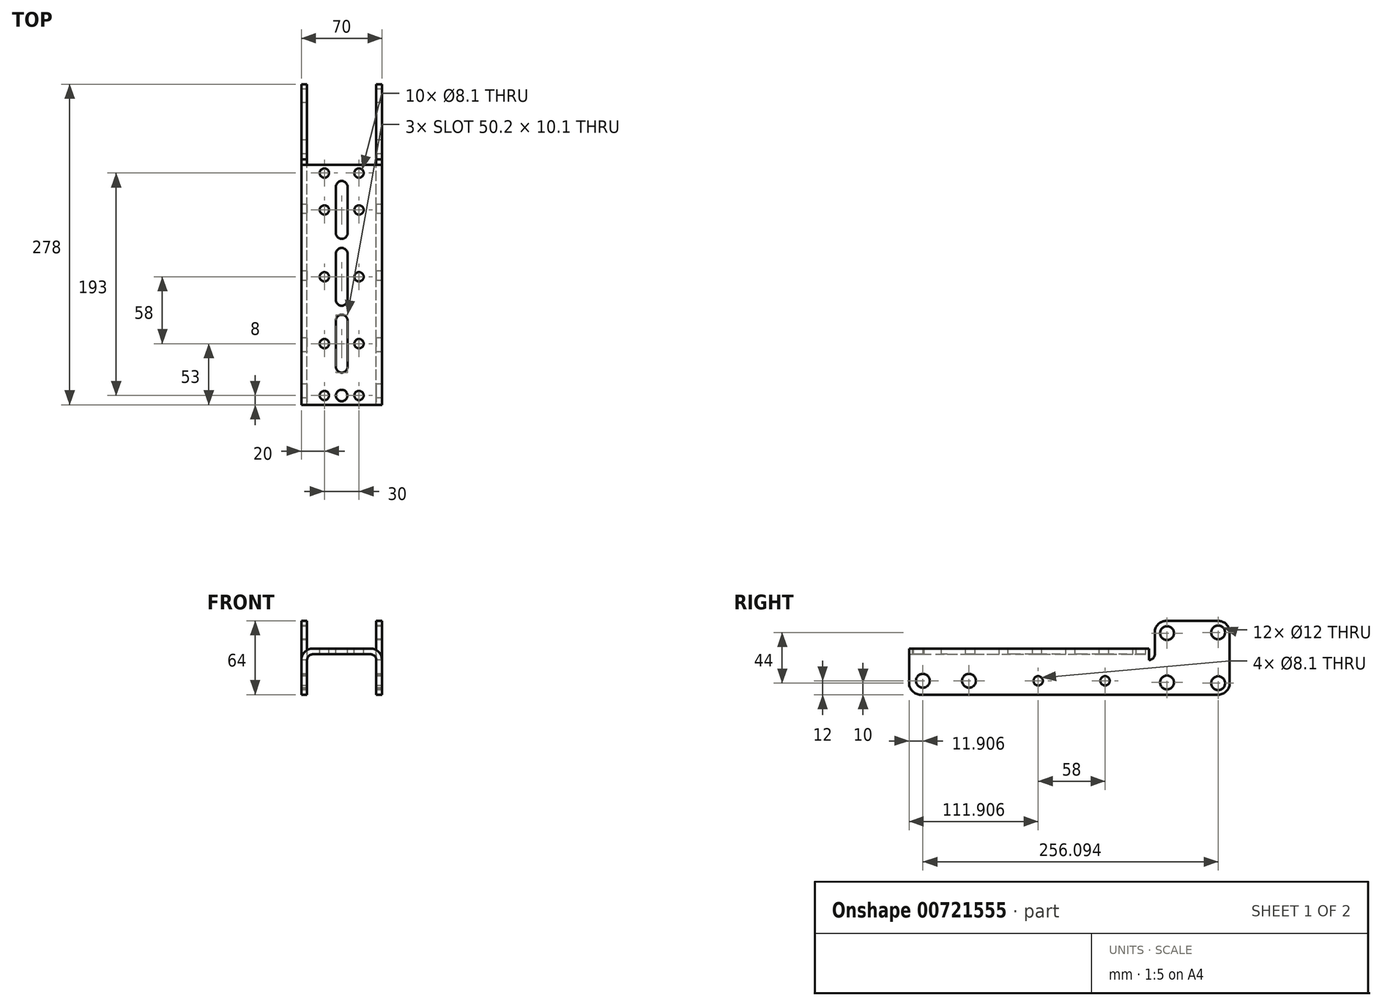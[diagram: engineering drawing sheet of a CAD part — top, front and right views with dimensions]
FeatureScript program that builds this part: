
annotation { "Feature Type Name" : "Feature", "Feature Type Description" : "" }
export const myFeature = defineFeature(function(context is Context, id is Id, definition is map)
    precondition{}
    {
        {
            var Q0;
            Q0=qCreatedBy(makeId("Front.planeOp"),FACE);
            var sketch = newSketch(context, id + "F0", { "sketchPlane" : qUnion([Q0])});
            skLineSegment(sketch, "E0.top", {"start": v(5, 35) * mm, "end": v(55, 35) * mm});
            skLineSegment(sketch, "E0.left", {"start": v(0, 0) * mm, "end": v(0, 30) * mm});
            skLineSegment(sketch, "E0.right", {"start": v(60, 0) * mm, "end": v(60, 30) * mm});
            skPoint(sketch, "E1.visualSharp", {"position": v(0, 35) * mm});
            skArc(sketch, "E1.filletArc", {"start": v(5, 35) * mm, "mid": v(1.46, 33.54) * mm, "end": v(0, 30) * mm});
            skPoint(sketch, "E2.visualSharp", {"position": v(60, 35) * mm});
            skArc(sketch, "E2.filletArc", {"start": v(60, 30) * mm, "mid": v(58.54, 33.54) * mm, "end": v(55, 35) * mm});
            skLineSegment(sketch, "E3.0", {"start": v(65, 0) * mm, "end": v(65, 30) * mm});
            skLineSegment(sketch, "E3.1", {"start": v(-5, 0) * mm, "end": v(-5, 30) * mm});
            skArc(sketch, "E3.2", {"start": v(5, 40) * mm, "mid": v(-2.07, 37.07) * mm, "end": v(-5, 30) * mm});
            skLineSegment(sketch, "E3.3", {"start": v(5, 40) * mm, "end": v(55, 40) * mm});
            skArc(sketch, "E3.4", {"start": v(65, 30) * mm, "mid": v(62.07, 37.07) * mm, "end": v(55, 40) * mm});
            skLineSegment(sketch, "E4", {"start": v(-5, 0) * mm, "end": v(0, 0) * mm});
            skLineSegment(sketch, "E5", {"start": v(60, 0) * mm, "end": v(65, 0) * mm});
            skSolve(sketch);
        }
        {
            var Q0;
            Q0 = qSketchRegion(id + "F0", true);
            extrude(context, id + "F1", {"entities" : qUnion([Q0]), "depth" : 208 * mm, "offsetDistance" : 25 * mm});
        }
        {
            var Q0;
            Q0=qCreatedBy(makeId("Right.planeOp"),FACE);
            var sketch = newSketch(context, id + "F2", { "sketchPlane" : qUnion([Q0])});
            skLineSegment(sketch, "E6", {"start": v(-208.1, 0) * mm, "end": v(-208.1, 12) * mm, "construction": true});
            skLineSegment(sketch, "E7", {"start": v(-208.1, 12) * mm, "end": v(0, 12) * mm, "construction": true});
            skLineSegment(sketch, "E8", {"start": v(-208.1, 12) * mm, "end": v(-196.1, 12) * mm, "construction": true});
            skCircle(sketch, "E9", {"center": v(-196.1, 12) * mm, "radius": 6 * mm});
            skLineSegment(sketch, "E10", {"start": v(-196.1, 12) * mm, "end": v(-156.1, 12) * mm, "construction": true});
            skCircle(sketch, "E11", {"center": v(-156.1, 12) * mm, "radius": 6 * mm});
            skLineSegment(sketch, "E12", {"start": v(-156.1, 12) * mm, "end": v(-96.1, 12) * mm});
            skLineSegment(sketch, "E13", {"start": v(-96.1, 12) * mm, "end": v(-38.1, 12) * mm});
            skCircle(sketch, "E14", {"center": v(-96.1, 12) * mm, "radius": 4.05 * mm});
            skCircle(sketch, "E15", {"center": v(-38.1, 12) * mm, "radius": 4.05 * mm});
            skSolve(sketch);
        }
        {
            var Q0;
            Q0 = qSketchRegion(id + "F2", true);
            extrude(context, id + "F3", {"entities" : qUnion([Q0]), "operationType" : NewBodyOperationType.REMOVE, "endBound" : BoundingType.THROUGH_ALL, "depth" : 25 * mm, "offsetDistance" : 25 * mm, "hasSecondDirection" : true, "secondDirectionBound" : SecondDirectionBoundingType.THROUGH_ALL, "secondDirectionOppositeDirection" : true, "secondDirectionDepth" : 25 * mm});
        }
        {
            var Q0;
            Q0=qCreatedBy(makeId("Front.planeOp"),FACE);
            var sketch = newSketch(context, id + "F4", { "sketchPlane" : qUnion([Q0])});
            skLineSegment(sketch, "E16", {"start": v(0, 0) * mm, "end": v(-5, 0) * mm});
            skLineSegment(sketch, "E17", {"start": v(-5, 0) * mm, "end": v(-5, 54) * mm});
            skLineSegment(sketch, "E18", {"start": v(0, 54) * mm, "end": v(0, 0) * mm});
            skLineSegment(sketch, "E19", {"start": v(0, 0) * mm, "end": v(30, 0) * mm, "construction": true});
            skPoint(sketch, "E20.newPointA", {"position": v(0, 59) * mm});
            skPoint(sketch, "E21.orphan", {"position": v(0, 64) * mm});
            skLineSegment(sketch, "E22", {"start": v(30, 64) * mm, "end": v(30, 28.75) * mm, "construction": true});
            skPoint(sketch, "E23.MirrorP", {"position": v(60, 64) * mm});
            skLineSegment(sketch, "E24.MirrorCS", {"start": v(60, 54) * mm, "end": v(60, 0) * mm});
            skLineSegment(sketch, "E25.MirrorCS", {"start": v(65, 0) * mm, "end": v(65, 54) * mm});
            skLineSegment(sketch, "E26.MirrorCS", {"start": v(60, 0) * mm, "end": v(65, 0) * mm});
            skLineSegment(sketch, "E27", {"start": v(-5, 54) * mm, "end": v(-5, 64) * mm});
            skLineSegment(sketch, "E28", {"start": v(-5, 64) * mm, "end": v(0, 64) * mm});
            skLineSegment(sketch, "E29", {"start": v(0, 54) * mm, "end": v(0, 64) * mm});
            skPoint(sketch, "E30.0.start.orphan", {"position": v(5, 64) * mm});
            skPoint(sketch, "E20.filletArc.start.orphan", {"position": v(5, 59) * mm});
            skPoint(sketch, "E31.MirrorCS.end.orphan", {"position": v(30, 64) * mm});
            skPoint(sketch, "E31.MirrorCS.start.orphan", {"position": v(55, 64) * mm});
            skPoint(sketch, "E32.MirrorCS.end.orphan", {"position": v(55, 59) * mm});
            skPoint(sketch, "E33.MirrorCS.end.orphan", {"position": v(65, 54) * mm});
            skPoint(sketch, "E34.MirrorCS.end.orphan", {"position": v(60, 54) * mm});
            skLineSegment(sketch, "E35.MirrorCS", {"start": v(65, 64) * mm, "end": v(60, 64) * mm});
            skLineSegment(sketch, "E36.MirrorCS", {"start": v(60, 54) * mm, "end": v(60, 64) * mm});
            skPoint(sketch, "E37.MirrorP", {"position": v(60, 59) * mm});
            skLineSegment(sketch, "E38.MirrorCS", {"start": v(65, 54) * mm, "end": v(65, 64) * mm});
            skSolve(sketch);
        }
        {
            var Q0;
            Q0 = qSketchRegion(id + "F4", true);
            extrude(context, id + "F5", {"entities" : qUnion([Q0]), "operationType" : NewBodyOperationType.ADD, "oppositeDirection" : true, "depth" : 70 * mm, "offsetDistance" : 25 * mm});
        }
        {
            var Q0;
            Q0=makeQuery(id+"F5.boolean.opBoolean","MERGE",FACE,{"derivedFrom":[makeQuery(id+"F1.opExtrude","SWEPT_FACE",FACE,{"disambiguationData":[OSD([sQuery(id+"F0.wireOp",EDGE,"E3.1")])]}),makeQuery(id+"F5.opExtrude","SWEPT_FACE",FACE,{"disambiguationData":[OSD([sQuery(id+"F4.wireOp",EDGE,"E17")])]})]});
            var sketch = newSketch(context, id + "F6", { "sketchPlane" : qUnion([Q0])});
            skLineSegment(sketch, "E39", {"start": v(-70, 0) * mm, "end": v(-70, 10) * mm});
            skLineSegment(sketch, "E40", {"start": v(-60, 0) * mm, "end": v(198, 0) * mm});
            skLineSegment(sketch, "E41", {"start": v(208, 10) * mm, "end": v(208, 30) * mm});
            skPoint(sketch, "E42.visualSharp", {"position": v(208, 0) * mm});
            skArc(sketch, "E42.filletArc", {"start": v(198, 0) * mm, "mid": v(205.07, 2.93) * mm, "end": v(208, 10) * mm});
            skPoint(sketch, "E43.visualSharp", {"position": v(-70, 0) * mm});
            skArc(sketch, "E43.filletArc", {"start": v(-70, 10) * mm, "mid": v(-67.07, 2.93) * mm, "end": v(-60, 0) * mm});
            skLineSegment(sketch, "E44", {"start": v(0, 30) * mm, "end": v(0, 30) * mm});
            skLineSegment(sketch, "E45", {"start": v(-5, 35) * mm, "end": v(-5, 54) * mm});
            skLineSegment(sketch, "E46", {"start": v(0, 63.5) * mm, "end": v(0, 30) * mm});
            skPoint(sketch, "E47.visualSharp", {"position": v(-5, 30) * mm});
            skArc(sketch, "E47.filletArc", {"start": v(-5, 35) * mm, "mid": v(-3.54, 31.46) * mm, "end": v(0, 30) * mm});
            skLineSegment(sketch, "E48", {"start": v(-5, 63.5) * mm, "end": v(-5, 71.81) * mm});
            skLineSegment(sketch, "E49", {"start": v(-5, 71.81) * mm, "end": v(0, 71.81) * mm});
            skLineSegment(sketch, "E50", {"start": v(0, 71.81) * mm, "end": v(0, 64) * mm});
            skLineSegment(sketch, "E51", {"start": v(-60, 64) * mm, "end": v(-15, 64) * mm});
            skLineSegment(sketch, "E52", {"start": v(-70, 54) * mm, "end": v(-70, 10) * mm});
            skPoint(sketch, "E53.visualSharp", {"position": v(-70, 64) * mm});
            skArc(sketch, "E53.filletArc", {"start": v(-60, 64) * mm, "mid": v(-67.07, 61.07) * mm, "end": v(-70, 54) * mm});
            skArc(sketch, "E54.filletArc", {"start": v(-5, 54) * mm, "mid": v(-7.93, 61.07) * mm, "end": v(-15, 64) * mm});
            skLineSegment(sketch, "E55", {"start": v(-70, 64) * mm, "end": v(-59.4, 53.4) * mm, "construction": true});
            skLineSegment(sketch, "E56", {"start": v(-15, 64) * mm, "end": v(-60, 64) * mm, "construction": true});
            skLineSegment(sketch, "E57", {"start": v(-37.5, 64) * mm, "end": v(-37.5, 0) * mm, "construction": true});
            skLineSegment(sketch, "E58", {"start": v(-37.5, 0) * mm, "end": v(-37.5, 32) * mm, "construction": true});
            skLineSegment(sketch, "E59", {"start": v(-37.5, 32) * mm, "end": v(-70, 32) * mm, "construction": true});
            skLineSegment(sketch, "E60.MirrorCS", {"start": v(-70, 0) * mm, "end": v(-59.4, 10.6) * mm, "construction": true});
            skLineSegment(sketch, "E61.MirrorCS", {"start": v(-5, 64) * mm, "end": v(-15.6, 53.4) * mm, "construction": true});
            skLineSegment(sketch, "E62.MirrorCS", {"start": v(-5, 0) * mm, "end": v(-15.6, 10.6) * mm, "construction": true});
            skCircle(sketch, "E63", {"center": v(-60, 54) * mm, "radius": 6 * mm});
            skCircle(sketch, "E64", {"center": v(-15.6, 53.4) * mm, "radius": 6 * mm});
            skCircle(sketch, "E65", {"center": v(-60, 10) * mm, "radius": 6 * mm});
            skCircle(sketch, "E66", {"center": v(-15.6, 10.6) * mm, "radius": 6 * mm});
            skSolve(sketch);
        }
        {
            var Q0;
            Q0 = qSketchRegion(id + "F6", true);
            var Q1;
            {var subQ0=sQuery(id+"F6.wireOp",EDGE,"E43.filletArc");Q1=makeQuery(id+"F6.imprint","IMPRINT",FACE,{"disambiguationData":[TD([[makeQuery(id+"F6.imprint","IMPRINT",EDGE,{"derivedFrom":subQ0}),-1.0]])]});}
            var Q2;
            {var subQ0=sQuery(id+"F6.wireOp",EDGE,"E42.filletArc");Q2=makeQuery(id+"F6.imprint","IMPRINT",FACE,{"disambiguationData":[TD([[makeQuery(id+"F6.imprint","IMPRINT",EDGE,{"derivedFrom":subQ0}),-1.0]])]});}
            var Q3;
            {var subQ0=sQuery(id+"F6.wireOp",EDGE,"E53.filletArc");Q3=makeQuery(id+"F6.imprint","IMPRINT",FACE,{"disambiguationData":[TD([[makeQuery(id+"F6.imprint","IMPRINT",EDGE,{"derivedFrom":subQ0}),-1.0]])]});}
            var Q4;
            Q4=makeQuery(id+"F6.imprint","IMPRINT",FACE,{"disambiguationData":[TD([[makeQuery(id+"F6.imprint","IMPRINT",EDGE,{"derivedFrom":sQuery(id+"F6.wireOp",EDGE,"E45")}),-1.0]])]});
            extrude(context, id + "F7", {"entities" : qUnion([Q0, Q1, Q2, Q3, Q4]), "operationType" : NewBodyOperationType.REMOVE, "endBound" : BoundingType.THROUGH_ALL, "oppositeDirection" : true, "depth" : 25 * mm, "offsetDistance" : 25 * mm});
        }
        {
            var Q0;
            Q0=makeQuery(id+"F1.opExtrude","SWEPT_FACE",FACE,{"disambiguationData":[OSD([sQuery(id+"F0.wireOp",EDGE,"E3.3")])]});
            var sketch = newSketch(context, id + "F8", { "sketchPlane" : qUnion([Q0])});
            skLineSegment(sketch, "E67", {"start": v(30, 0) * mm, "end": v(30, -208) * mm, "construction": true});
            skLineSegment(sketch, "E68", {"start": v(30, -208) * mm, "end": v(30, -200) * mm, "construction": true});
            skLineSegment(sketch, "E69", {"start": v(30, -200) * mm, "end": v(15, -200) * mm, "construction": true});
            skLineSegment(sketch, "E70", {"start": v(15, -200) * mm, "end": v(15, -155) * mm, "construction": true});
            skLineSegment(sketch, "E71", {"start": v(15, -155) * mm, "end": v(15, -97) * mm, "construction": true});
            skLineSegment(sketch, "E72", {"start": v(15, -97) * mm, "end": v(15, -39) * mm, "construction": true});
            skLineSegment(sketch, "E73", {"start": v(15, -39) * mm, "end": v(15, -7) * mm, "construction": true});
            skCircle(sketch, "E74", {"center": v(15, -7) * mm, "radius": 4.05 * mm});
            skCircle(sketch, "E75", {"center": v(15, -39) * mm, "radius": 4.05 * mm});
            skCircle(sketch, "E76", {"center": v(15, -97) * mm, "radius": 4.05 * mm});
            skCircle(sketch, "E77", {"center": v(15, -155) * mm, "radius": 4.05 * mm});
            skCircle(sketch, "E78", {"center": v(15, -200) * mm, "radius": 4.05 * mm});
            skCircle(sketch, "E79", {"center": v(30, -200) * mm, "radius": 5 * mm});
            skLineSegment(sketch, "E80", {"start": v(15, -97) * mm, "end": v(30, -97) * mm});
            skLineSegment(sketch, "E81", {"start": v(30, -97) * mm, "end": v(30, -76.95) * mm});
            skLineSegment(sketch, "E82", {"start": v(15, -39) * mm, "end": v(30, -39) * mm, "construction": true});
            skLineSegment(sketch, "E83", {"start": v(30, -39) * mm, "end": v(30, -18.95) * mm, "construction": true});
            skArc(sketch, "E84", {"start": v(35.05, -18.95) * mm, "mid": v(30, -13.9) * mm, "end": v(24.95, -18.95) * mm});
            skArc(sketch, "E85", {"start": v(35.05, -76.95) * mm, "mid": v(30, -71.9) * mm, "end": v(24.95, -76.95) * mm});
            skArc(sketch, "E86.MirrorC", {"start": v(35.05, -59.05) * mm, "mid": v(30, -64.1) * mm, "end": v(24.95, -59.05) * mm});
            skArc(sketch, "E87.MirrorC", {"start": v(35.05, -117.05) * mm, "mid": v(30, -122.1) * mm, "end": v(24.95, -117.05) * mm});
            skLineSegment(sketch, "E88", {"start": v(15, -126) * mm, "end": v(41.58, -126) * mm, "construction": true});
            skLineSegment(sketch, "E89.MirrorC", {"start": v(35.05, -233.05) * mm, "end": v(35.05, -233.05) * mm});
            skArc(sketch, "E90.MirrorC", {"start": v(35.05, -175.05) * mm, "mid": v(30, -180.1) * mm, "end": v(24.95, -175.05) * mm});
            skArc(sketch, "E91.MirrorC", {"start": v(35.05, -134.95) * mm, "mid": v(30, -129.9) * mm, "end": v(24.95, -134.95) * mm});
            skLineSegment(sketch, "E92", {"start": v(35.05, -18.95) * mm, "end": v(35.05, -59.05) * mm});
            skLineSegment(sketch, "E93", {"start": v(24.95, -59.05) * mm, "end": v(24.95, -18.95) * mm});
            skLineSegment(sketch, "E94", {"start": v(24.95, -76.95) * mm, "end": v(24.95, -117.05) * mm});
            skLineSegment(sketch, "E95", {"start": v(35.05, -117.05) * mm, "end": v(35.05, -76.95) * mm});
            skLineSegment(sketch, "E96.MirrorCS", {"start": v(24.95, -175.05) * mm, "end": v(24.95, -134.95) * mm});
            skLineSegment(sketch, "E97.MirrorCS", {"start": v(35.05, -134.95) * mm, "end": v(35.05, -175.05) * mm});
            skCircle(sketch, "E98.MirrorC", {"center": v(45, -7) * mm, "radius": 4.05 * mm});
            skCircle(sketch, "E99.MirrorC", {"center": v(45, -39) * mm, "radius": 4.05 * mm});
            skCircle(sketch, "E100.MirrorC", {"center": v(45, -97) * mm, "radius": 4.05 * mm});
            skCircle(sketch, "E101.MirrorC", {"center": v(45, -155) * mm, "radius": 4.05 * mm});
            skCircle(sketch, "E102.MirrorC", {"center": v(45, -200) * mm, "radius": 4.05 * mm});
            skPoint(sketch, "E103.orphan", {"position": v(24.95, -233.05) * mm});
            skPoint(sketch, "E104.orphan", {"position": v(35.05, -192.95) * mm});
            skPoint(sketch, "E105.orphan", {"position": v(24.95, -192.95) * mm});
            skSolve(sketch);
        }
        {
            var Q0;
            Q0 = qSketchRegion(id + "F8", true);
            extrude(context, id + "F9", {"entities" : qUnion([Q0]), "operationType" : NewBodyOperationType.REMOVE, "endBound" : BoundingType.THROUGH_ALL, "oppositeDirection" : true, "depth" : 25 * mm, "offsetDistance" : 25 * mm});
        }
    });
